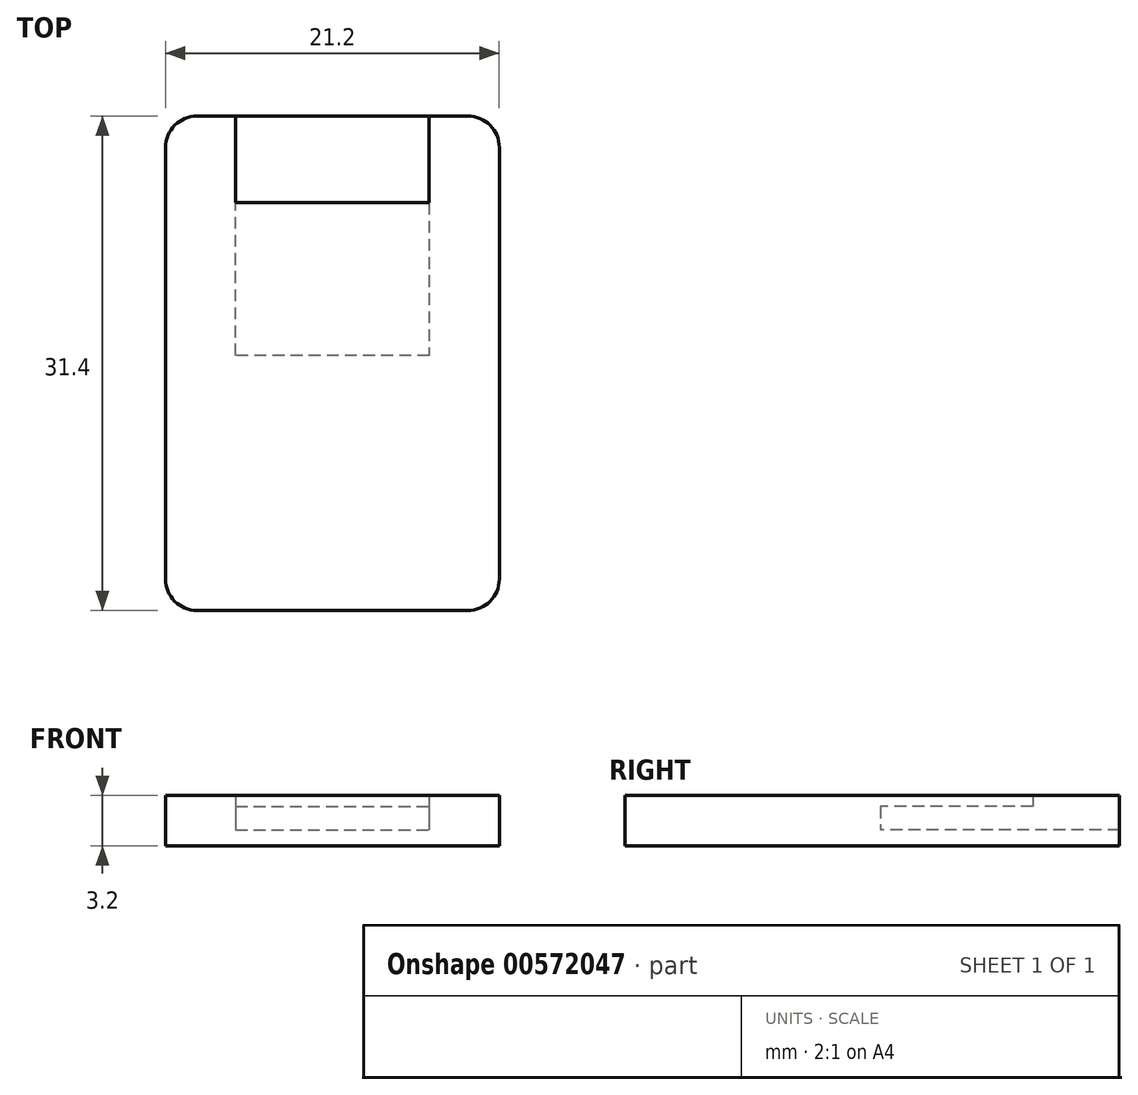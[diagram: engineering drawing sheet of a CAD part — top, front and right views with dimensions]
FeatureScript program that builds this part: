
annotation { "Feature Type Name" : "Feature", "Feature Type Description" : "" }
export const myFeature = defineFeature(function(context is Context, id is Id, definition is map)
    precondition{}
    {
        {
            var Q0;
            Q0=qCreatedBy(makeId("Top.planeOp"),FACE);
            var sketch = newSketch(context, id + "F0", { "sketchPlane" : qUnion([Q0])});
            skLineSegment(sketch, "E0", {"start": v(-48.89, 49.74) * mm, "end": v(-27.69, 49.74) * mm});
            skLineSegment(sketch, "E1", {"start": v(-48.89, 49.74) * mm, "end": v(-48.89, 18.34) * mm});
            skLineSegment(sketch, "E2", {"start": v(-48.89, 18.34) * mm, "end": v(-27.69, 18.34) * mm});
            skLineSegment(sketch, "E3", {"start": v(-27.69, 18.34) * mm, "end": v(-27.69, 49.74) * mm});
            skLineSegment(sketch, "E4", {"start": v(-32.14, 49.74) * mm, "end": v(-32.14, 34.54) * mm});
            skLineSegment(sketch, "E5", {"start": v(-32.14, 34.54) * mm, "end": v(-44.44, 34.54) * mm});
            skLineSegment(sketch, "E6", {"start": v(-44.44, 34.54) * mm, "end": v(-44.44, 49.74) * mm});
            skLineSegment(sketch, "E7", {"start": v(-44.44, 44.24) * mm, "end": v(-32.14, 44.24) * mm});
            skSolve(sketch);
        }
        {
            var Q0;
            Q0=makeQuery(id+"F0.imprint","IMPRINT",FACE,{"disambiguationData":[TD([[makeQuery(id+"F0.imprint","IMPRINT",EDGE,{"derivedFrom":sQuery(id+"F0.wireOp",EDGE,"E0")}),-1.0]])]});
            var Q1;
            {var subQ0=sQuery(id+"F0.wireOp",EDGE,"E5");Q1=makeQuery(id+"F0.imprint","IMPRINT",FACE,{"disambiguationData":[TD([[makeQuery(id+"F0.imprint","IMPRINT",EDGE,{"derivedFrom":subQ0}),-1.0]])]});}
            extrude(context, id + "F1", {"entities" : qUnion([Q0, Q1]), "depth" : 3.2 * mm, "offsetDistance" : 25 * mm});
        }
        {
            var Q0;
            Q0=makeQuery(id+"F1.opExtrude","SWEPT_EDGE",EDGE,{"disambiguationData":[OSD([sQuery(id+"F0.wireOp",EDGE,"E2"),sQuery(id+"F0.wireOp",EDGE,"E3")])]});
            var Q1;
            Q1=makeQuery(id+"F1.opExtrude","SWEPT_EDGE",EDGE,{"disambiguationData":[OSD([sQuery(id+"F0.wireOp",EDGE,"E0"),sQuery(id+"F0.wireOp",EDGE,"E3")])]});
            var Q2;
            Q2=makeQuery(id+"F1.opExtrude","SWEPT_EDGE",EDGE,{"disambiguationData":[OSD([sQuery(id+"F0.wireOp",EDGE,"E1"),sQuery(id+"F0.wireOp",EDGE,"E2")])]});
            var Q3;
            Q3=makeQuery(id+"F1.opExtrude","SWEPT_EDGE",EDGE,{"disambiguationData":[OSD([sQuery(id+"F0.wireOp",EDGE,"E0"),sQuery(id+"F0.wireOp",EDGE,"E1")])]});
            fillet(context, id + "F2", {"entities" : qUnion([Q0, Q1, Q2, Q3]), "radius" : 2 * mm, "tangentPropagation" : true, "allowEdgeOverflow" : false});
        }
        {
            var Q0;
            {var subQ0=sQuery(id+"F0.wireOp",EDGE,"E5");Q0=makeQuery(id+"F0.imprint","IMPRINT",FACE,{"disambiguationData":[TD([[makeQuery(id+"F0.imprint","IMPRINT",EDGE,{"derivedFrom":subQ0}),-1.0]])]});}
            extrude(context, id + "F3", {"entities" : qUnion([Q0]), "operationType" : NewBodyOperationType.REMOVE, "depth" : 2.5 * mm, "offsetDistance" : 25 * mm});
        }
        {
            var Q0;
            {var subQ0=sQuery(id+"F0.wireOp",EDGE,"E5");Q0=makeQuery(id+"F0.imprint","IMPRINT",FACE,{"disambiguationData":[TD([[makeQuery(id+"F0.imprint","IMPRINT",EDGE,{"derivedFrom":subQ0}),-1.0]])]});}
            var Q1;
            {var subQ5=sQuery(id+"F0.wireOp",EDGE,"E7");Q1=makeQuery(id+"F0.imprint","IMPRINT",FACE,{"disambiguationData":[TD([[makeQuery(id+"F0.imprint","IMPRINT",EDGE,{"derivedFrom":subQ5}),1.0]])]});}
            extrude(context, id + "F4", {"entities" : qUnion([Q0, Q1]), "operationType" : NewBodyOperationType.ADD, "depth" : 1 * mm, "offsetDistance" : 25 * mm});
        }
    });
